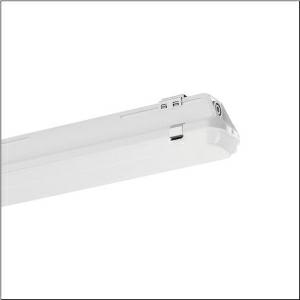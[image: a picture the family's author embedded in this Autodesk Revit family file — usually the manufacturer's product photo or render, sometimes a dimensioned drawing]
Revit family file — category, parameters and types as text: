
# Revit family: monsun_r__21_51fb10mp380b_1725
name_source: partatom
category: Lighting Fixtures
units: mm (PartAtom-declared; Revit-internal decimal feet)

## family parameters
Cut with Voids When Loaded = No
Host = Face
Light Source = No
Part Type = Normal
Room Calculation Point = No
Round Connector Dimension = Use Diameter
Shared = No

## types (1)
- --- (1 x LED, 8190 lm, 59.7 W, 3000K)
    Apparent Load = 60 VA
    CIE Flux Codes = 47 77 93 94 100
    Color Rendering = 80
    Color Temperature = 3000K
    Default Elevation = 1800 mm
    Description = Monsun® 21, damp-proof luminaire, chain hanger, primary optical cover: enclosure, of PMMA, light emission: direct distribution, primary light characteristic: symmetric, installation type: suspended mounting, surface-mounted, horizontal mounting, vertical mounting, LED, rated luminous flux: 8.190lm, luminous efficacy: 153lm/W, light colour: 830, colour temperature: 3000K, control gear: ON/OFF Multilumen, with terminal, 3-pole, max. 2.5mm², mains connection: 220..240V, AC, 50/60Hz, rated input power: 54W, housing, of glass-fibre reinforced polyester, uncoated, bright grey, incl. chain hanger, length: 1.590mm, width: 90mm, height: 88mm, clip for enclosure, of stainless steel (V2A), ceiling mounting element, of stainless steel (V2A), chain hanger, of stainless steel (V2A), protection rating (complete): IP66, insulation class (complete): insulation class I (protective earthing), certification: CE, ENEC, VDE, UKCA, protection symbol: D, impact resistance: IK04, permissible operating ambient temperature: -25..+35°C, standard: EN 50419, EN 60598-2-1, no direct snow, no direct sun, no direct rain, for indoor or canopied outdoor use, corresponds to IFS (International Featured Standards) requirements for safety and quality in the food industry, contact your sales advisor before using the luminaires in applications with unclear chemical exposure, large temperature fluctuations or condensation-forming humidity, LABS conformity tested according to VDMA 24364:2018-05, packaging unit: 1 piece
    Height = 89 mm
    Lamp = 1 x LED
    Lamp Light Flux = 8190 lm
    Lamp Power = 59.7 W
    Lamp count = 1
    Length = 1590 mm
    Luminous efficacy = 137 lm/W
    Manufacturer = Siteco
    ModVariant = No
    Model = 51FB10MP380B
    Mounting Place = Ceiling
    Mounting Type = Surface mounted
    Number of Poles = 1
    OnlyDefault = Yes
    Power Factor = 1
    Product Name = Monsun® 21
    Product group = damp-proof luminaire
    ProductGroupID = 300
    Protection Class = Protection class I
    Protection Degree = IP 66
    RLX_Detail_Level = 1
    RLX_Emergency_Light_Flux = 0 lm
    RLX_Emergency_Type = 0
    RLX_Emergency_Type_DB = No
    RlxData = <blob elided: 89801 chars, md5=a384310c>
    Socket = socket
    Standby Power = 0 W
    System Light Flux = 8190 lm
    System Power = 60 W
    Type Comments = factory setting: luminous flux: 100 % | (A | C | E) | 134 mA
    Type Image = l_1319656.jpg
    URL = http://relux.com
    VarID = @adj_146826
    Voltage = 0 V
    Weight = 0.00 kg
    Width = 90 mm

## geometry (parser evidence)
native form markers: Blend x4, Sweep x11
no freeform markers — native parametric forms only
